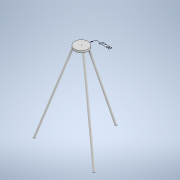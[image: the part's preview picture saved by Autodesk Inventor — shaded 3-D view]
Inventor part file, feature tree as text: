
AUTODESK INVENTOR PART (.ipt)
format: ipt  version: 2021.2 (Build 252289000, 289)  size: 120,832 bytes
history: native  units: in
note: dims shown in document units (in); Inventor stores cm internally (conversion verified against a paired STEP export)
features: sketch x4, other x2, extrude x2, plane x1, loft x1, pattern_circular x1
ambient origin geometry x8: Origin, YZ Plane, XZ Plane, XY Plane, X Axis, Y Axis, Z Axis, Center Point
bodies: Body1 (feature_tree)
feature tree (11):
  other  "Annotations"
  sketch  "Sketch3"  dims[d16=1.0in d17=18.0in]
  plane  "Work Plane3"
  loft  "Loft2"
  pattern_circular  "Circular Pattern1"  Angle=90.0deg  [1 undecoded]
  extrude  "Extrusion1"  TaperAngle=0.0deg  [1 undecoded]
  extrude  "Extrusion2"  Depth=1.0in TaperAngle=360.0deg
  sketch  "Sketch4"  dims[d18=44.0in]
  sketch  "Sketch5"  dims[d19=3.0in]
  sketch  "Sketch6"  dims[d20=1.0in d21=0.0in d22=90.0deg d23=0.0in d24=90.0deg d25=1.1811in d26=360.0deg d28=7.0in d29=1.0in d30=0.0in d31=0.25in d32=0.0in d33=0.0in d34=1.7567in d35=7.0in]
  other  "Diameter Dimension 1"
note: 2 required parameter values undecoded (feature->parameter linkage not recoverable at this tier; creation-order binding heuristic only, values carry confidence <= 0.55)
